# Revit family: 185-19-1
name_source: partatom
category: Plumbing Fixtures
revit_build: Autodesk Revit 2014 (Build: 20130308_1515(x64)
units: mm (PartAtom-declared; Revit-internal decimal feet)

## types (1)
- 185-19-1
    CW Connection = Yes
    Certification = http://www.helvex.com.mx
    Chrome = Brass Chromed
    Compliance = NOM-005-CONAGUA-1996
    Connection = 1" Feeding Connection
    Description = Exposed Urinal Flush Valve With Lever
    Documentation = http://www.helvex.com.mx
    Features = Lever With Antibacterial Coating, Left Or Right Connection
    Flow = 1 Lt Per Flush
    Instructive = http://www.helvex.com.mx
    Manufacturer = HELVEX
    Max. Working Pressure = 85.3 psi
    Min. Working Pressure = 14.2 psi
    Model = 185-19-1
    Note = Feeding Pipe Must Be 1 ¼" And Connect a  ¼" - 1" Reductor to Stop Valve
    Type Comments = Flush Valves
    URL = http://www.helvex.com.mx

## geometry (parser evidence)
native form markers: Sweep x1
no freeform markers — native parametric forms only
